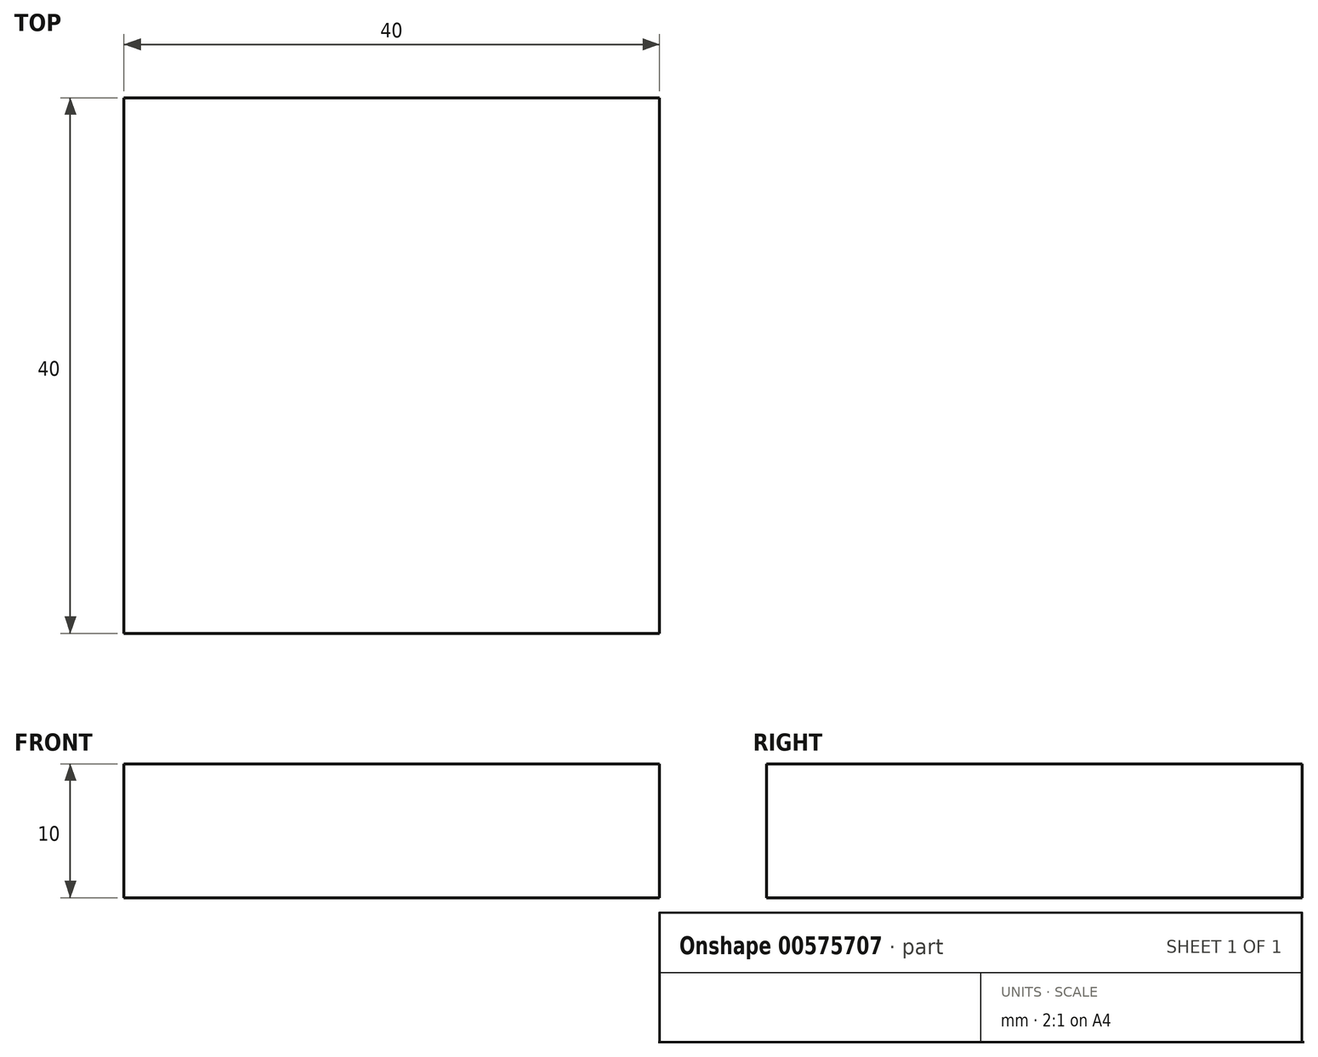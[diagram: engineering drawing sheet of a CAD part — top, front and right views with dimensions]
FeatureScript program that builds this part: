
annotation { "Feature Type Name" : "Feature", "Feature Type Description" : "" }
export const myFeature = defineFeature(function(context is Context, id is Id, definition is map)
    precondition{}
    {
        {
            var Q0;
            Q0=qCreatedBy(makeId("Top.planeOp"),FACE);
            var sketch = newSketch(context, id + "F0", { "sketchPlane" : qUnion([Q0])});
            skLineSegment(sketch, "E0.bottom", {"start": v(-20, 20) * mm, "end": v(20, 20) * mm});
            skLineSegment(sketch, "E0.top", {"start": v(-20, -20) * mm, "end": v(20, -20) * mm});
            skLineSegment(sketch, "E0.left", {"start": v(-20, 20) * mm, "end": v(-20, -20) * mm});
            skLineSegment(sketch, "E0.right", {"start": v(20, 20) * mm, "end": v(20, -20) * mm});
            skPoint(sketch, "E0.middle", {"position": v(0, 0) * mm});
            skSolve(sketch);
        }
        {
            var Q0;
            Q0 = qSketchRegion(id + "F0", true);
            extrude(context, id + "F1", {"entities" : qUnion([Q0]), "depth" : 10 * mm, "offsetDistance" : 25 * mm});
        }
    });
